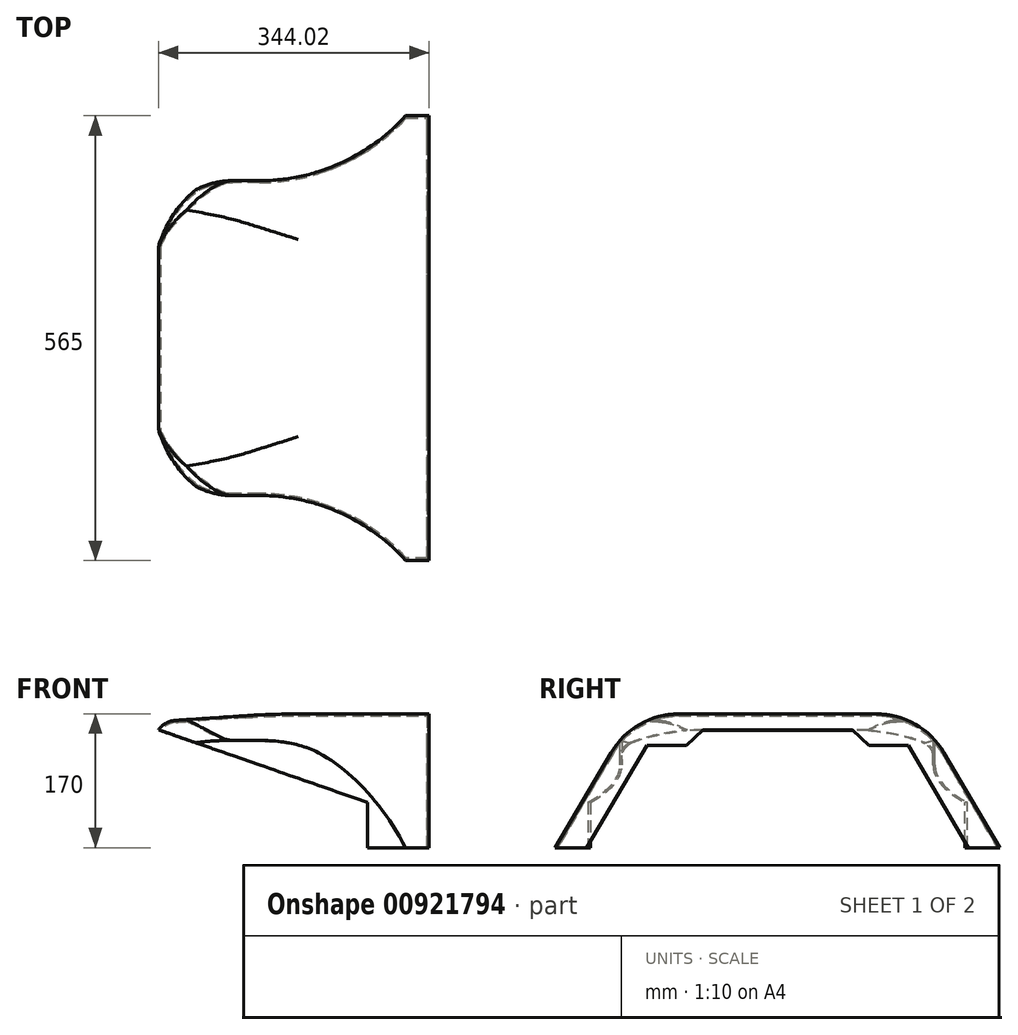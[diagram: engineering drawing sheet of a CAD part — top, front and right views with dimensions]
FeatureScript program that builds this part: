
annotation { "Feature Type Name" : "Feature", "Feature Type Description" : "" }
export const myFeature = defineFeature(function(context is Context, id is Id, definition is map)
    precondition{}
    {
        {
            var Q0;
            Q0=qCreatedBy(makeId("Top.planeOp"),FACE);
            var sketch = newSketch(context, id + "F0", { "sketchPlane" : qUnion([Q0])});
            skLineSegment(sketch, "E0.bottom", {"start": v(175, -282.5) * mm, "end": v(-175, -282.5) * mm, "construction": true});
            skLineSegment(sketch, "E0.top", {"start": v(175, 282.5) * mm, "end": v(-175, 282.5) * mm, "construction": true});
            skLineSegment(sketch, "E0.left", {"start": v(175, -282.5) * mm, "end": v(175, 282.5) * mm});
            skLineSegment(sketch, "E0.right", {"start": v(-175, -282.5) * mm, "end": v(-175, 282.5) * mm, "construction": true});
            skPoint(sketch, "E0.middle", {"position": v(0, 0) * mm});
            skLineSegment(sketch, "E1", {"start": v(-175, 200) * mm, "end": v(75, 200) * mm});
            skLineSegment(sketch, "E2", {"start": v(75, 200) * mm, "end": v(145, 282.5) * mm});
            skLineSegment(sketch, "E3", {"start": v(0, 0) * mm, "end": v(68.04, 0) * mm, "construction": true});
            skLineSegment(sketch, "E4.MirrorCS", {"start": v(75, -200) * mm, "end": v(145, -282.5) * mm});
            skLineSegment(sketch, "E5.MirrorCS", {"start": v(-175, -200) * mm, "end": v(75, -200) * mm});
            skLineSegment(sketch, "E6", {"start": v(175, 282.5) * mm, "end": v(145, 282.5) * mm});
            skLineSegment(sketch, "E7", {"start": v(175, -282.5) * mm, "end": v(145, -282.5) * mm});
            skLineSegment(sketch, "E8", {"start": v(-175, -200) * mm, "end": v(-175, 200) * mm});
            skSolve(sketch);
        }
        {
            var Q0;
            Q0 = qSketchRegion(id + "F0", true);
            extrude(context, id + "F1", {"entities" : qUnion([Q0]), "oppositeDirection" : true, "depth" : 170 * mm, "offsetDistance" : 25 * mm});
        }
        {
            var Q0;
            Q0=makeQuery(id+"F1.opExtrude","CAP_EDGE",EDGE,{"disambiguationData":[OSD([sQuery(id+"F0.wireOp",EDGE,"E8")])],"isStart":true});
            chamfer(context, id + "F2", {"entities" : qUnion([Q0]), "chamferType" : ChamferType.TWO_OFFSETS, "width1" : 10 * mm, "oppositeDirection" : false, "width2" : 150 * mm});
        }
        {
            var Q0;
            {var subQ0=sQuery(id+"F0.wireOp",EDGE,"E8");Q0=makeQuery(id+"F2.opChamfer","BLEND_EDGE",EDGE,{"blendedFrom":[makeQuery(id+"F1.opExtrude","CAP_EDGE",EDGE,{"disambiguationData":[OSD([subQ0])],"isStart":true}),makeQuery(id+"F1.opExtrude","CAP_FACE",FACE,{"disambiguationData":[OSD([sQuery(id+"F0.wireOp",EDGE,"E0.left"),sQuery(id+"F0.wireOp",EDGE,"E1"),sQuery(id+"F0.wireOp",EDGE,"E2"),sQuery(id+"F0.wireOp",EDGE,"E4.MirrorCS"),sQuery(id+"F0.wireOp",EDGE,"E5.MirrorCS"),sQuery(id+"F0.wireOp",EDGE,"E6"),sQuery(id+"F0.wireOp",EDGE,"E7"),subQ0])],"isStart":true})],"blendedInto":[makeQuery(id+"F1.opExtrude","CAP_FACE",FACE,{"disambiguationData":[OSD([sQuery(id+"F0.wireOp",EDGE,"E0.left"),sQuery(id+"F0.wireOp",EDGE,"E1"),sQuery(id+"F0.wireOp",EDGE,"E2"),sQuery(id+"F0.wireOp",EDGE,"E4.MirrorCS"),sQuery(id+"F0.wireOp",EDGE,"E5.MirrorCS"),sQuery(id+"F0.wireOp",EDGE,"E6"),sQuery(id+"F0.wireOp",EDGE,"E7"),subQ0])],"isStart":true})]});}
            fillet(context, id + "F3", {"entities" : qUnion([Q0]), "radius" : 1000 * mm, "tangentPropagation" : true, "allowEdgeOverflow" : false});
        }
        {
            var Q0;
            Q0=makeQuery(id+"F1.opExtrude","SWEPT_EDGE",EDGE,{"disambiguationData":[OSD([sQuery(id+"F0.wireOp",EDGE,"E4.MirrorCS"),sQuery(id+"F0.wireOp",EDGE,"E5.MirrorCS")])]});
            var Q1;
            Q1=makeQuery(id+"F1.opExtrude","SWEPT_EDGE",EDGE,{"disambiguationData":[OSD([sQuery(id+"F0.wireOp",EDGE,"E1"),sQuery(id+"F0.wireOp",EDGE,"E2")])]});
            fillet(context, id + "F4", {"entities" : qUnion([Q0, Q1]), "radius" : 250 * mm, "tangentPropagation" : true, "allowEdgeOverflow" : false});
        }
        {
            var Q0;
            Q0=makeQuery(id+"F1.opExtrude","CAP_EDGE",EDGE,{"disambiguationData":[OSD([sQuery(id+"F0.wireOp",EDGE,"E7")])],"isStart":true});
            var Q1;
            Q1=makeQuery(id+"F1.opExtrude","CAP_EDGE",EDGE,{"disambiguationData":[OSD([sQuery(id+"F0.wireOp",EDGE,"E6")])],"isStart":true});
            chamfer(context, id + "F5", {"entities" : qUnion([Q0, Q1]), "chamferType" : ChamferType.TWO_OFFSETS, "width1" : 170 * mm, "oppositeDirection" : false, "width2" : 100 * mm, "tangentPropagation" : true});
        }
        {
            var Q0;
            Q0=makeQuery(id+"F1.opExtrude","SWEPT_EDGE",EDGE,{"disambiguationData":[OSD([sQuery(id+"F0.wireOp",EDGE,"E5.MirrorCS"),sQuery(id+"F0.wireOp",EDGE,"E8")])]});
            var Q1;
            Q1=makeQuery(id+"F5.opChamfer","BLEND_EDGE",EDGE,{"blendedFrom":[makeQuery(id+"F1.opExtrude","CAP_EDGE",EDGE,{"disambiguationData":[OSD([sQuery(id+"F0.wireOp",EDGE,"E7")])],"isStart":true}),makeQuery(id+"F1.opExtrude","SWEPT_FACE",FACE,{"disambiguationData":[OSD([sQuery(id+"F0.wireOp",EDGE,"E8")])]})],"blendedInto":[makeQuery(id+"F1.opExtrude","SWEPT_FACE",FACE,{"disambiguationData":[OSD([sQuery(id+"F0.wireOp",EDGE,"E8")])]})]});
            var Q2;
            Q2=makeQuery(id+"F5.opChamfer","BLEND_EDGE",EDGE,{"blendedFrom":[makeQuery(id+"F1.opExtrude","CAP_EDGE",EDGE,{"disambiguationData":[OSD([sQuery(id+"F0.wireOp",EDGE,"E6")])],"isStart":true}),makeQuery(id+"F1.opExtrude","SWEPT_FACE",FACE,{"disambiguationData":[OSD([sQuery(id+"F0.wireOp",EDGE,"E8")])]})],"blendedInto":[makeQuery(id+"F1.opExtrude","SWEPT_FACE",FACE,{"disambiguationData":[OSD([sQuery(id+"F0.wireOp",EDGE,"E8")])]})]});
            var Q3;
            Q3=makeQuery(id+"F1.opExtrude","SWEPT_EDGE",EDGE,{"disambiguationData":[OSD([sQuery(id+"F0.wireOp",EDGE,"E1"),sQuery(id+"F0.wireOp",EDGE,"E8")])]});
            fillet(context, id + "F6", {"entities" : qUnion([Q0, Q1, Q2, Q3]), "radius" : 100 * mm, "tangentPropagation" : true, "allowEdgeOverflow" : false});
        }
        {
            var Q0;
            {var subQ0=sQuery(id+"F0.wireOp",EDGE,"E8");Q0=makeQuery(id+"F2.opChamfer","BLEND_EDGE",EDGE,{"blendedFrom":[makeQuery(id+"F1.opExtrude","CAP_EDGE",EDGE,{"disambiguationData":[OSD([subQ0])],"isStart":true}),makeQuery(id+"F1.opExtrude","SWEPT_FACE",FACE,{"disambiguationData":[OSD([subQ0])]})],"blendedInto":[makeQuery(id+"F1.opExtrude","SWEPT_FACE",FACE,{"disambiguationData":[OSD([subQ0])]})]});}
            fillet(context, id + "F7", {"entities" : qUnion([Q0]), "radius" : 30 * mm, "allowEdgeOverflow" : false});
        }
        {
            var Q0;
            Q0=makeQuery(id+"F1.opExtrude","SWEPT_FACE",FACE,{"disambiguationData":[OSD([sQuery(id+"F0.wireOp",EDGE,"E0.left")])]});
            var sketch = newSketch(context, id + "F8", { "sketchPlane" : qUnion([Q0])});
            skLineSegment(sketch, "E9", {"start": v(-242.5, -170) * mm, "end": v(-166.03, -40) * mm});
            skLineSegment(sketch, "E10", {"start": v(-166.03, -40) * mm, "end": v(166.03, -40) * mm});
            skLineSegment(sketch, "E11", {"start": v(166.03, -40) * mm, "end": v(242.5, -170) * mm});
            skLineSegment(sketch, "E12", {"start": v(242.5, -170) * mm, "end": v(-242.5, -170) * mm});
            skSolve(sketch);
        }
        {
            var Q0;
            Q0=qCreatedBy(makeId("Front.planeOp"),FACE);
            cPlane(context, id + "F9", {"entities" : qUnion([Q0]), "cplaneType" : CPlaneType.OFFSET, "offset" : 400 * mm, "width" : 150 * mm, "height" : 150 * mm});
        }
        {
            var Q0;
            Q0=qCreatedBy(id+"F9.planeOp",FACE);
            var sketch = newSketch(context, id + "F10", { "sketchPlane" : qUnion([Q0])});
            skLineSegment(sketch, "E13", {"start": v(-178.23, -173.36) * mm, "end": v(96.34, -173.36) * mm});
            skLineSegment(sketch, "E14", {"start": v(96.34, -173.36) * mm, "end": v(96.34, -112.28) * mm});
            skLineSegment(sketch, "E15", {"start": v(96.34, -112.28) * mm, "end": v(-177.68, -17.1) * mm});
            skLineSegment(sketch, "E16", {"start": v(-177.68, -17.1) * mm, "end": v(-178.23, -173.36) * mm});
            skSolve(sketch);
        }
        {
            var Q0;
            {var subQ0=sQuery(id+"F0.wireOp",EDGE,"E6");Q0=makeQuery(id+"F5.opChamfer","BLEND_EDGE",EDGE,{"blendedFrom":[makeQuery(id+"F1.opExtrude","CAP_EDGE",EDGE,{"disambiguationData":[OSD([subQ0])],"isStart":true}),makeQuery(id+"F1.opExtrude","CAP_FACE",FACE,{"disambiguationData":[OSD([sQuery(id+"F0.wireOp",EDGE,"E0.left"),sQuery(id+"F0.wireOp",EDGE,"E1"),sQuery(id+"F0.wireOp",EDGE,"E2"),sQuery(id+"F0.wireOp",EDGE,"E4.MirrorCS"),sQuery(id+"F0.wireOp",EDGE,"E5.MirrorCS"),subQ0,sQuery(id+"F0.wireOp",EDGE,"E7"),sQuery(id+"F0.wireOp",EDGE,"E8")])],"isStart":true})],"blendedInto":[makeQuery(id+"F1.opExtrude","CAP_FACE",FACE,{"disambiguationData":[OSD([sQuery(id+"F0.wireOp",EDGE,"E0.left"),sQuery(id+"F0.wireOp",EDGE,"E1"),sQuery(id+"F0.wireOp",EDGE,"E2"),sQuery(id+"F0.wireOp",EDGE,"E4.MirrorCS"),sQuery(id+"F0.wireOp",EDGE,"E5.MirrorCS"),subQ0,sQuery(id+"F0.wireOp",EDGE,"E7"),sQuery(id+"F0.wireOp",EDGE,"E8")])],"isStart":true})]});}
            var Q1;
            {var subQ0=sQuery(id+"F0.wireOp",EDGE,"E7");Q1=makeQuery(id+"F5.opChamfer","BLEND_EDGE",EDGE,{"blendedFrom":[makeQuery(id+"F1.opExtrude","CAP_EDGE",EDGE,{"disambiguationData":[OSD([subQ0])],"isStart":true}),makeQuery(id+"F1.opExtrude","CAP_FACE",FACE,{"disambiguationData":[OSD([sQuery(id+"F0.wireOp",EDGE,"E0.left"),sQuery(id+"F0.wireOp",EDGE,"E1"),sQuery(id+"F0.wireOp",EDGE,"E2"),sQuery(id+"F0.wireOp",EDGE,"E4.MirrorCS"),sQuery(id+"F0.wireOp",EDGE,"E5.MirrorCS"),sQuery(id+"F0.wireOp",EDGE,"E6"),subQ0,sQuery(id+"F0.wireOp",EDGE,"E8")])],"isStart":true})],"blendedInto":[makeQuery(id+"F1.opExtrude","CAP_FACE",FACE,{"disambiguationData":[OSD([sQuery(id+"F0.wireOp",EDGE,"E0.left"),sQuery(id+"F0.wireOp",EDGE,"E1"),sQuery(id+"F0.wireOp",EDGE,"E2"),sQuery(id+"F0.wireOp",EDGE,"E4.MirrorCS"),sQuery(id+"F0.wireOp",EDGE,"E5.MirrorCS"),sQuery(id+"F0.wireOp",EDGE,"E6"),subQ0,sQuery(id+"F0.wireOp",EDGE,"E8")])],"isStart":true})]});}
            fillet(context, id + "F11", {"entities" : qUnion([Q0, Q1]), "radius" : 100 * mm, "allowEdgeOverflow" : false});
        }
        {
            var Q0;
            Q0=makeQuery(id+"F1.opExtrude","CAP_FACE",FACE,{"disambiguationData":[OSD([sQuery(id+"F0.wireOp",EDGE,"E0.left"),sQuery(id+"F0.wireOp",EDGE,"E1"),sQuery(id+"F0.wireOp",EDGE,"E2"),sQuery(id+"F0.wireOp",EDGE,"E4.MirrorCS"),sQuery(id+"F0.wireOp",EDGE,"E5.MirrorCS"),sQuery(id+"F0.wireOp",EDGE,"E6"),sQuery(id+"F0.wireOp",EDGE,"E7"),sQuery(id+"F0.wireOp",EDGE,"E8")])],"isStart":false});
            shell(context, id + "F12", {"entities" : qUnion([Q0]), "thickness" : 2.5 * mm});
        }
        {
            var Q0;
            Q0 = qSketchRegion(id + "F10", true);
            extrude(context, id + "F13", {"entities" : qUnion([Q0]), "operationType" : NewBodyOperationType.REMOVE, "oppositeDirection" : true, "depth" : 900 * mm, "offsetDistance" : 25 * mm});
        }
        {
            var Q0;
            Q0=makeQuery(id+"F8.imprint","IMPRINT",FACE,{"disambiguationData":[TD([[makeQuery(id+"F8.imprint","IMPRINT",EDGE,{"derivedFrom":sQuery(id+"F8.wireOp",EDGE,"E9")}),-1.0]])]});
            extrude(context, id + "F14", {"entities" : qUnion([Q0]), "operationType" : NewBodyOperationType.REMOVE, "oppositeDirection" : true, "depth" : 25 * mm, "offsetDistance" : 25 * mm});
        }
        {
            var Q0;
            Q0=makeQuery(id+"F1.opExtrude","SWEPT_FACE",FACE,{"disambiguationData":[OSD([sQuery(id+"F0.wireOp",EDGE,"E0.left")])]});
            var sketch = newSketch(context, id + "F15", { "sketchPlane" : qUnion([Q0])});
            skLineSegment(sketch, "E17", {"start": v(-116.03, -40) * mm, "end": v(-95, -20) * mm});
            skLineSegment(sketch, "E18", {"start": v(-95, -20) * mm, "end": v(95, -20) * mm});
            skLineSegment(sketch, "E19", {"start": v(95, -20) * mm, "end": v(116.03, -40) * mm});
            skSolve(sketch);
        }
        {
            var Q0;
            {var subQ0=sQuery(id+"F15.wireOp",EDGE,"E17");Q0=makeQuery(id+"F15.imprint","IMPRINT",FACE,{"disambiguationData":[TD([[makeQuery(id+"F15.imprint","IMPRINT",EDGE,{"derivedFrom":subQ0}),-1.0]])]});}
            extrude(context, id + "F16", {"entities" : qUnion([Q0]), "operationType" : NewBodyOperationType.REMOVE, "oppositeDirection" : true, "depth" : 25 * mm, "offsetDistance" : 25 * mm});
        }
    });
